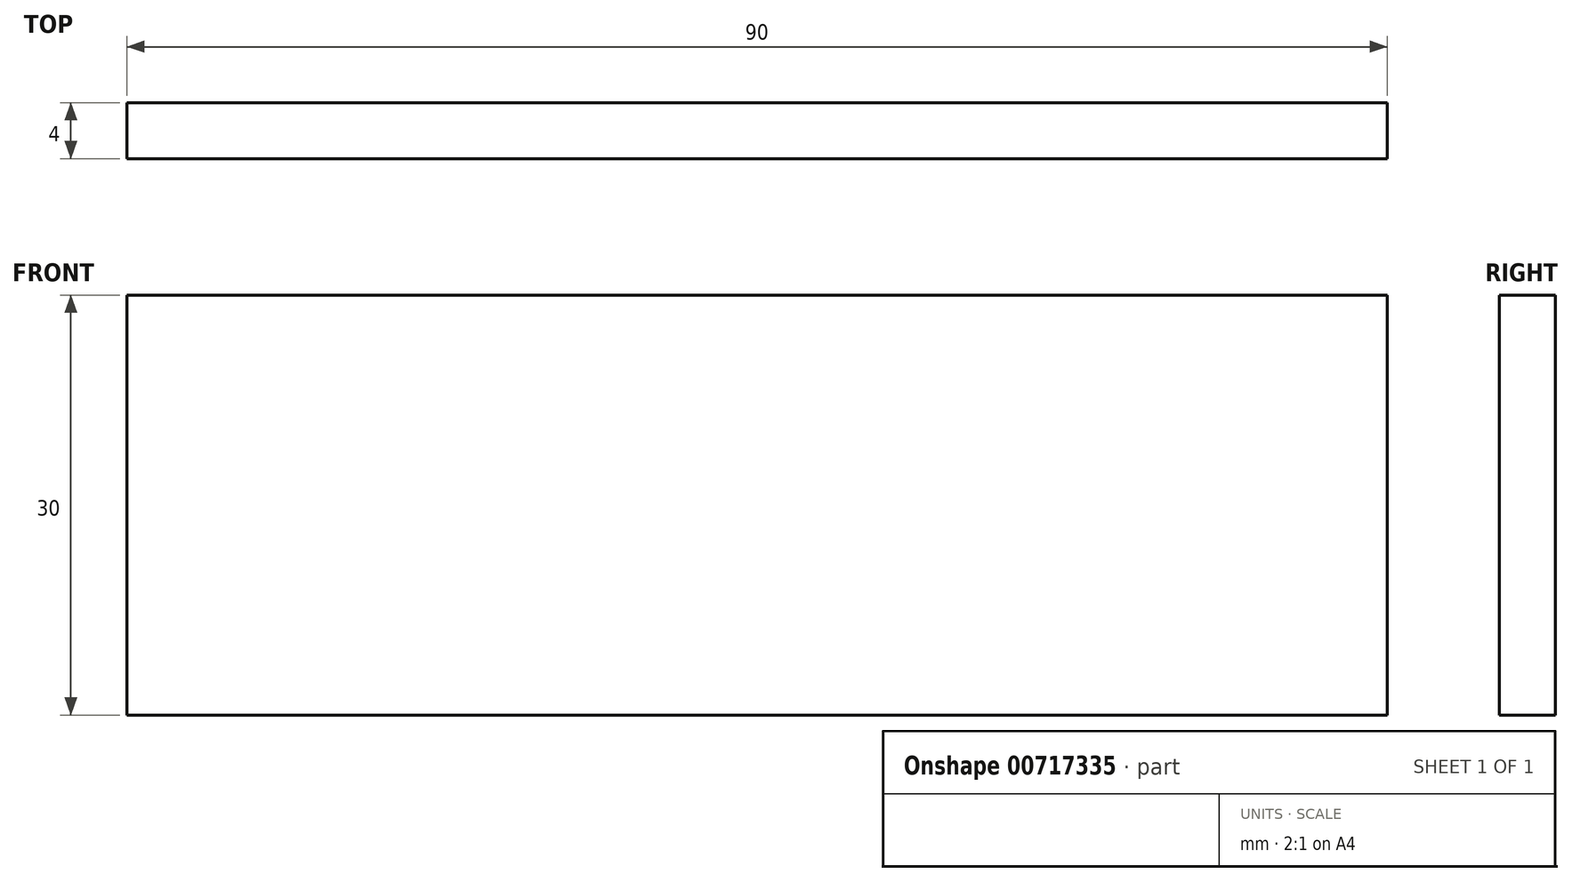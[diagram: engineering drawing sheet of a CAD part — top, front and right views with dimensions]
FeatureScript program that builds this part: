
annotation { "Feature Type Name" : "Feature", "Feature Type Description" : "" }
export const myFeature = defineFeature(function(context is Context, id is Id, definition is map)
    precondition{}
    {
        {
            var Q0;
            Q0=qCreatedBy(makeId("Top.planeOp"),FACE);
            var sketch = newSketch(context, id + "F0", { "sketchPlane" : qUnion([Q0])});
            skLineSegment(sketch, "E0.bottom", {"start": v(0, 0) * mm, "end": v(90, 0) * mm});
            skLineSegment(sketch, "E0.top", {"start": v(0, 4) * mm, "end": v(90, 4) * mm});
            skLineSegment(sketch, "E0.left", {"start": v(0, 0) * mm, "end": v(0, 4) * mm});
            skLineSegment(sketch, "E0.right", {"start": v(90, 0) * mm, "end": v(90, 4) * mm});
            skSolve(sketch);
        }
        {
            var Q0;
            Q0 = qSketchRegion(id + "F0", true);
            extrude(context, id + "F1", {"entities" : qUnion([Q0]), "depth" : 30 * mm, "offsetDistance" : 25 * mm});
        }
    });
